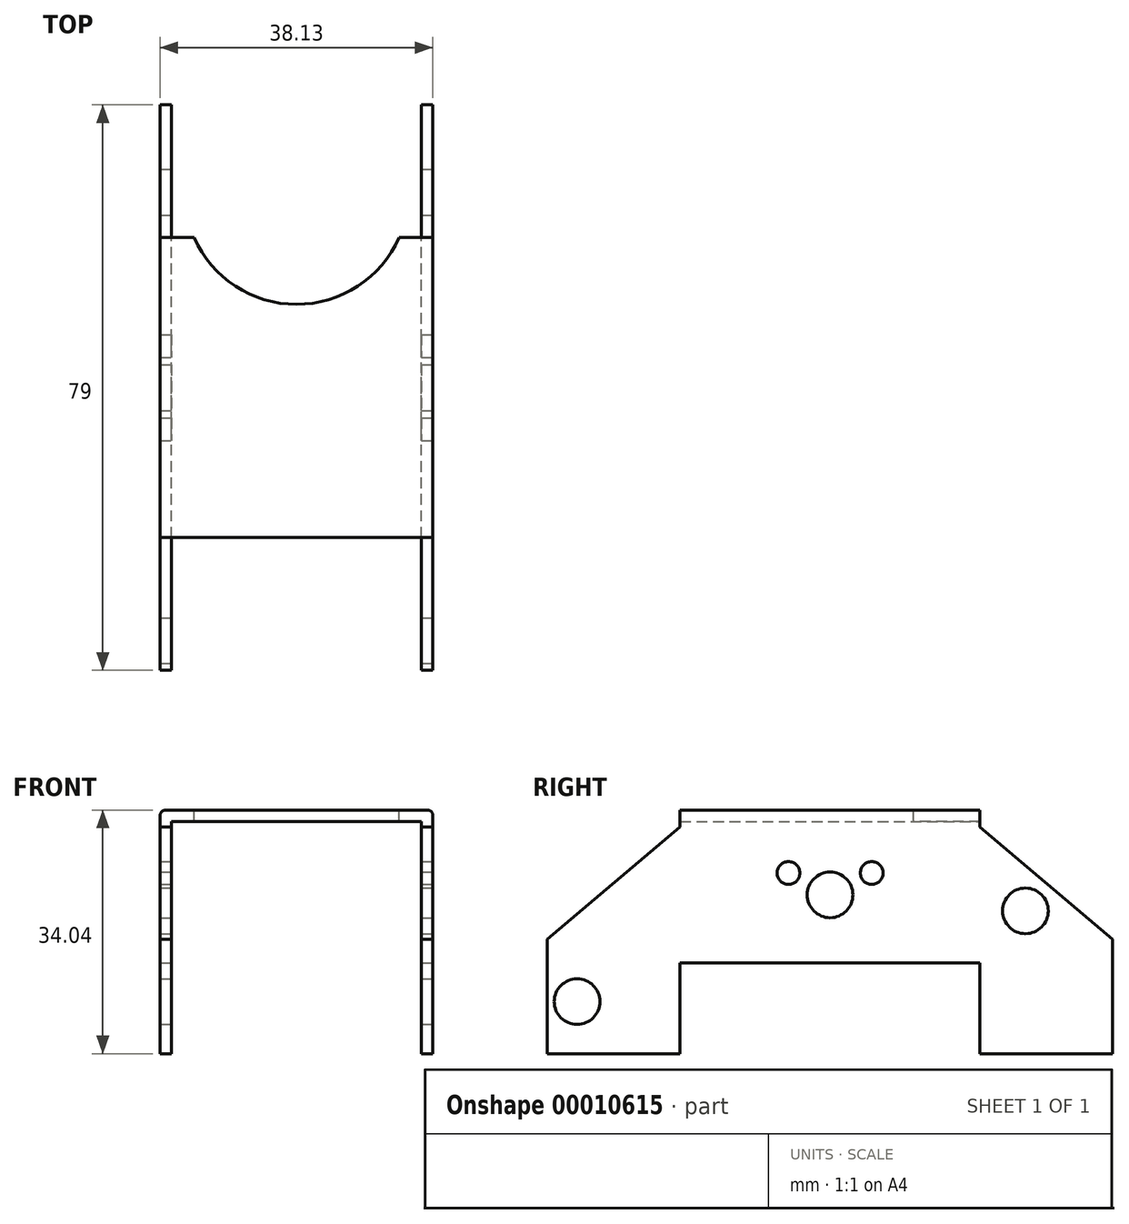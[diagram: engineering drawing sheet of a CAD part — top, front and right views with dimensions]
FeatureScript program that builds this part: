
annotation { "Feature Type Name" : "Feature", "Feature Type Description" : "" }
export const myFeature = defineFeature(function(context is Context, id is Id, definition is map)
    precondition{}
    {
        {
            var Q0;
            Q0=qCreatedBy(makeId("Right.planeOp"),FACE);
            var sketch = newSketch(context, id + "F0", { "sketchPlane" : qUnion([Q0])});
            skLineSegment(sketch, "E0.rect.bottom", {"start": v(39.5, -17.02) * mm, "end": v(20.96, -17.02) * mm});
            skLineSegment(sketch, "E0.rect.top", {"start": v(20.95, 14.63) * mm, "end": v(-20.96, 14.63) * mm});
            skLineSegment(sketch, "E0.rect.left", {"start": v(39.5, -17.02) * mm, "end": v(39.5, -1.02) * mm});
            skLineSegment(sketch, "E0.rect.right", {"start": v(-39.5, -17.02) * mm, "end": v(-39.5, -1.02) * mm});
            skPoint(sketch, "E0.rect.middle", {"position": v(0, 0) * mm});
            skLineSegment(sketch, "E1", {"start": v(-39.5, -4.32) * mm, "end": v(39.5, -4.32) * mm, "construction": true});
            skLineSegment(sketch, "E2", {"start": v(-20.96, 14.63) * mm, "end": v(-20.96, -17.02) * mm, "construction": true});
            skLineSegment(sketch, "E3", {"start": v(20.95, 14.63) * mm, "end": v(20.96, -17.02) * mm, "construction": true});
            skLineSegment(sketch, "E4", {"start": v(-39.5, -1.02) * mm, "end": v(39.5, -1.02) * mm, "construction": true});
            skLineSegment(sketch, "E5", {"start": v(39.5, -1.02) * mm, "end": v(20.95, 14.63) * mm});
            skLineSegment(sketch, "E6", {"start": v(-39.5, -1.02) * mm, "end": v(-20.96, 14.63) * mm});
            skLineSegment(sketch, "E7.trimOffspring", {"start": v(-20.95, -17.02) * mm, "end": v(-39.5, -17.02) * mm});
            skLineSegment(sketch, "E8", {"start": v(-20.96, -17.02) * mm, "end": v(-20.96, -4.32) * mm});
            skLineSegment(sketch, "E9", {"start": v(-20.96, -4.32) * mm, "end": v(20.96, -4.32) * mm});
            skLineSegment(sketch, "E10", {"start": v(20.96, -4.32) * mm, "end": v(20.96, -17.02) * mm});
            skLineSegment(sketch, "E11.bottom", {"start": v(-20.96, 14.63) * mm, "end": v(20.95, 14.63) * mm});
            skLineSegment(sketch, "E11.top", {"start": v(-20.96, 15.42) * mm, "end": v(20.95, 15.42) * mm});
            skLineSegment(sketch, "E11.left", {"start": v(-20.96, 14.63) * mm, "end": v(-20.96, 15.42) * mm});
            skLineSegment(sketch, "E11.right", {"start": v(20.95, 14.63) * mm, "end": v(20.95, 15.42) * mm});
            skLineSegment(sketch, "E12.top", {"start": v(-20.96, 17.02) * mm, "end": v(20.95, 17.02) * mm});
            skLineSegment(sketch, "E12.left", {"start": v(-20.96, 15.42) * mm, "end": v(-20.96, 17.02) * mm});
            skLineSegment(sketch, "E12.right", {"start": v(20.95, 15.42) * mm, "end": v(20.95, 17.02) * mm});
            skCircle(sketch, "E13", {"center": v(0, 5.16) * mm, "radius": 3.19 * mm});
            skCircle(sketch, "E14", {"center": v(-35.36, -9.76) * mm, "radius": 3.19 * mm});
            skCircle(sketch, "E15", {"center": v(5.82, 8.21) * mm, "radius": 1.59 * mm});
            skLineSegment(sketch, "E16", {"start": v(0, 17.02) * mm, "end": v(0, -4.32) * mm, "construction": true});
            skCircle(sketch, "E17.0.MirrorC", {"center": v(-5.82, 8.21) * mm, "radius": 1.59 * mm});
            skCircle(sketch, "E18", {"center": v(27.3, 2.93) * mm, "radius": 3.19 * mm});
            skSolve(sketch);
        }
        {
            var Q0;
            Q0=qSketchRegion(id+"F0",true);
            extrude(context, id + "F1", {"entities" : qUnion([Q0]), "oppositeDirection" : true, "depth" : 1.57 * mm});
        }
        {
            var Q0;
            Q0=qSketchRegion(id+"F0",true);
            extrude(context, id + "F2", {"entities" : qUnion([Q0]), "operationType" : NewBodyOperationType.ADD, "oppositeDirection" : true, "depth" : 1.6 * mm});
        }
        {
            var Q0;
            Q0=makeQuery(id+"F2.opExtrude","CAP_FACE",FACE,{"disambiguationData":[OSD([sQuery(id+"F0.wireOp",EDGE,"E0.rect.bottom"),sQuery(id+"F0.wireOp",EDGE,"E0.rect.left"),sQuery(id+"F0.wireOp",EDGE,"E0.rect.right"),sQuery(id+"F0.wireOp",EDGE,"E5"),sQuery(id+"F0.wireOp",EDGE,"E6"),sQuery(id+"F0.wireOp",EDGE,"E7.trimOffspring"),sQuery(id+"F0.wireOp",EDGE,"E8"),sQuery(id+"F0.wireOp",EDGE,"E9"),sQuery(id+"F0.wireOp",EDGE,"E10"),sQuery(id+"F0.wireOp",EDGE,"E11.left"),sQuery(id+"F0.wireOp",EDGE,"E11.right"),sQuery(id+"F0.wireOp",EDGE,"E12.top"),sQuery(id+"F0.wireOp",EDGE,"E12.left"),sQuery(id+"F0.wireOp",EDGE,"E12.right")])],"isStart":false});
            var sketch = newSketch(context, id + "F3", { "sketchPlane" : qUnion([Q0])});
            skLineSegment(sketch, "E19.0", {"start": v(20.96, 17.02) * mm, "end": v(-20.95, 17.02) * mm});
            skLineSegment(sketch, "E20.0", {"start": v(20.96, 15.42) * mm, "end": v(-20.95, 15.42) * mm});
            skLineSegment(sketch, "E21.0", {"start": v(-20.95, 15.42) * mm, "end": v(-20.95, 17.02) * mm});
            skLineSegment(sketch, "E22.0", {"start": v(20.96, 15.42) * mm, "end": v(20.96, 17.02) * mm});
            skSolve(sketch);
        }
        {
            var Q0;
            Q0=qSketchRegion(id+"F3",true);
            extrude(context, id + "F4", {"entities" : qUnion([Q0]), "operationType" : NewBodyOperationType.ADD, "depth" : 34.92 * mm});
        }
        {
            var Q0;
            Q0=makeQuery(id+"F4.opExtrude","CAP_FACE",FACE,{"disambiguationData":[OSD([sQuery(id+"F3.wireOp",EDGE,"E19.0"),sQuery(id+"F3.wireOp",EDGE,"E20.0"),sQuery(id+"F3.wireOp",EDGE,"E21.0"),sQuery(id+"F3.wireOp",EDGE,"E22.0")])],"isStart":false});
            var sketch = newSketch(context, id + "F5", { "sketchPlane" : qUnion([Q0])});
            skLineSegment(sketch, "E23.0", {"start": v(20.96, -4.32) * mm, "end": v(-20.96, -4.32) * mm});
            skLineSegment(sketch, "E24.0", {"start": v(20.96, -17.02) * mm, "end": v(20.96, -4.32) * mm});
            skLineSegment(sketch, "E25.0", {"start": v(20.95, -17.02) * mm, "end": v(39.5, -17.02) * mm});
            skLineSegment(sketch, "E26.0", {"start": v(39.5, -17.02) * mm, "end": v(39.5, -1.02) * mm});
            skLineSegment(sketch, "E27.0", {"start": v(39.5, -1.02) * mm, "end": v(20.96, 14.63) * mm});
            skLineSegment(sketch, "E28.0", {"start": v(20.96, 14.63) * mm, "end": v(20.96, 15.42) * mm});
            skLineSegment(sketch, "E29.0", {"start": v(20.96, 15.42) * mm, "end": v(20.96, 17.02) * mm});
            skLineSegment(sketch, "E30.0", {"start": v(20.96, 17.02) * mm, "end": v(-20.95, 17.02) * mm});
            skLineSegment(sketch, "E31.0", {"start": v(-20.95, 15.42) * mm, "end": v(-20.95, 17.02) * mm});
            skLineSegment(sketch, "E32.0", {"start": v(-20.95, 14.63) * mm, "end": v(-20.95, 15.42) * mm});
            skLineSegment(sketch, "E33.0", {"start": v(-39.5, -1.02) * mm, "end": v(-20.95, 14.63) * mm});
            skLineSegment(sketch, "E34.0", {"start": v(-39.5, -17.02) * mm, "end": v(-39.5, -1.02) * mm});
            skLineSegment(sketch, "E35.0", {"start": v(-39.5, -17.02) * mm, "end": v(-20.96, -17.02) * mm});
            skLineSegment(sketch, "E36.0", {"start": v(-20.96, -4.32) * mm, "end": v(-20.96, -17.02) * mm});
            skCircle(sketch, "E37.0", {"center": v(-5.82, 8.21) * mm, "radius": 1.59 * mm});
            skCircle(sketch, "E38.0", {"center": v(0, 5.16) * mm, "radius": 3.19 * mm});
            skCircle(sketch, "E39.0", {"center": v(5.82, 8.21) * mm, "radius": 1.59 * mm});
            skCircle(sketch, "E40.0", {"center": v(35.36, -9.76) * mm, "radius": 3.19 * mm});
            skLineSegment(sketch, "E41.0", {"start": v(0, 17.02) * mm, "end": v(0, -4.32) * mm, "construction": true});
            skCircle(sketch, "E42.0", {"center": v(-27.3, 2.93) * mm, "radius": 3.19 * mm});
            skSolve(sketch);
        }
        {
            var Q0;
            Q0=qSketchRegion(id+"F5",true);
            extrude(context, id + "F6", {"entities" : qUnion([Q0]), "operationType" : NewBodyOperationType.ADD, "depth" : 1.6 * mm});
        }
        {
            var Q0;
            Q0=makeQuery(id+"F4.opExtrude","CAP_EDGE",EDGE,{"disambiguationData":[OSD([sQuery(id+"F3.wireOp",EDGE,"E20.0")])],"isStart":true});
            var Q1;
            Q1=makeQuery(id+"F4.opExtrude","CAP_EDGE",EDGE,{"disambiguationData":[OSD([sQuery(id+"F3.wireOp",EDGE,"E20.0")])],"isStart":false});
            var Q2;
            Q2=makeQuery(id+"F6.opExtrude","CAP_EDGE",EDGE,{"disambiguationData":[OSD([sQuery(id+"F5.wireOp",EDGE,"E30.0")])],"isStart":false});
            var Q3;
            Q3=makeQuery(id+"F1.opExtrude","CAP_EDGE",EDGE,{"disambiguationData":[OSD([sQuery(id+"F0.wireOp",EDGE,"E12.top")])],"isStart":true});
            fillet(context, id + "F7", {"entities" : qUnion([Q0, Q1, Q2, Q3]), "radius" : 0.79 * mm, "tangentPropagation" : true, "allowEdgeOverflow" : false});
        }
        {
            var Q0;
            {var subQ0=sQuery(id+"F0.wireOp",EDGE,"E12.top");Q0=makeQuery(id+"F6.boolean.opBoolean","MERGE",FACE,{"derivedFrom":[makeQuery(id+"F4.boolean.opBoolean","MERGE",FACE,{"derivedFrom":[makeQuery(id+"F2.boolean.opBoolean","MERGE",FACE,{"derivedFrom":[makeQuery(id+"F1.opExtrude","SWEPT_FACE",FACE,{"disambiguationData":[OSD([subQ0])]}),makeQuery(id+"F2.opExtrude","SWEPT_FACE",FACE,{"disambiguationData":[OSD([subQ0])]})]}),makeQuery(id+"F4.opExtrude","SWEPT_FACE",FACE,{"disambiguationData":[OSD([sQuery(id+"F3.wireOp",EDGE,"E19.0")])]})]}),makeQuery(id+"F6.opExtrude","SWEPT_FACE",FACE,{"disambiguationData":[OSD([sQuery(id+"F5.wireOp",EDGE,"E30.0")])]})]});}
            var sketch = newSketch(context, id + "F8", { "sketchPlane" : qUnion([Q0])});
            skLineSegment(sketch, "E43", {"start": v(-19.06, -20.96) * mm, "end": v(-19.06, 40.35) * mm, "construction": true});
            skCircle(sketch, "E44", {"center": v(-19.06, 27.3) * mm, "radius": 15.67 * mm});
            skSolve(sketch);
        }
        {
            var Q0;
            Q0=qSketchRegion(id+"F8",true);
            extrude(context, id + "F9", {"entities" : qUnion([Q0]), "operationType" : NewBodyOperationType.REMOVE, "endBound" : BoundingType.THROUGH_ALL, "oppositeDirection" : true, "depth" : 25.4 * mm});
        }
    });
